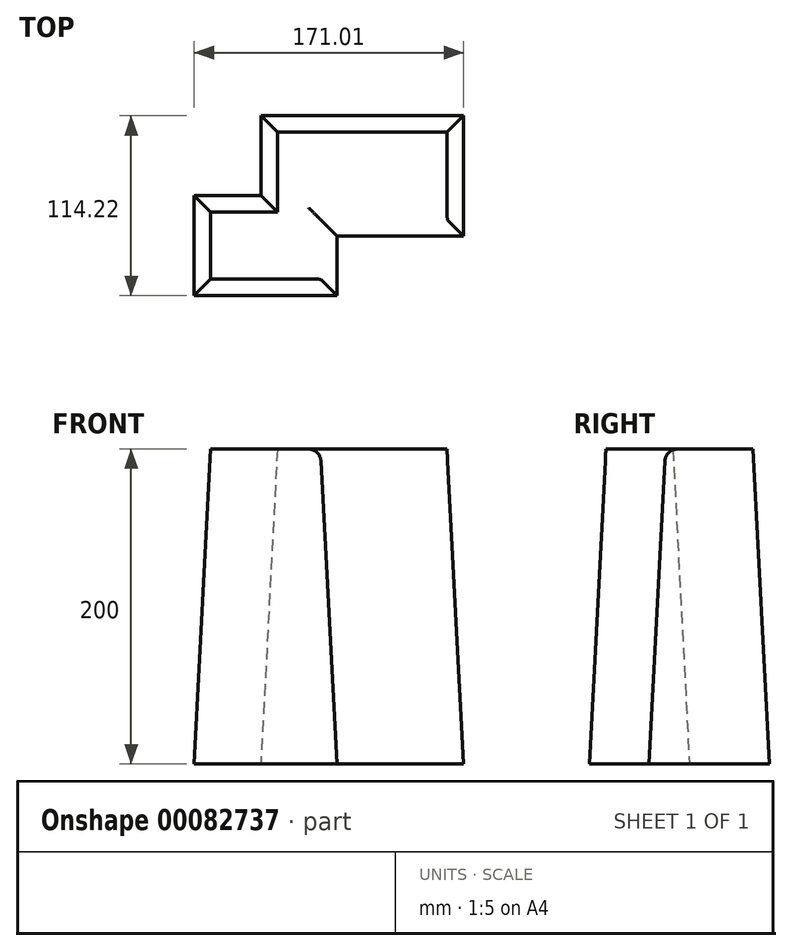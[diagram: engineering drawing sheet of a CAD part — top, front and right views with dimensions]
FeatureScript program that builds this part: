
annotation { "Feature Type Name" : "Feature", "Feature Type Description" : "" }
export const myFeature = defineFeature(function(context is Context, id is Id, definition is map)
    precondition{}
    {
        {
            var Q0;
            Q0=qCreatedBy(makeId("Top.planeOp"),FACE);
            var sketch = newSketch(context, id + "F0", { "sketchPlane" : qUnion([Q0])});
            skLineSegment(sketch, "E0.bottom", {"start": v(0, 0) * mm, "end": v(90.56, 0) * mm});
            skLineSegment(sketch, "E0.top", {"start": v(0, 63.51) * mm, "end": v(42.33, 63.51) * mm});
            skLineSegment(sketch, "E0.left", {"start": v(0, 0) * mm, "end": v(0, 63.51) * mm});
            skLineSegment(sketch, "E0.right", {"start": v(90.56, 0) * mm, "end": v(90.56, 37.82) * mm});
            skLineSegment(sketch, "E1.bottom", {"start": v(90.56, 37.82) * mm, "end": v(171.01, 37.82) * mm});
            skLineSegment(sketch, "E1.top", {"start": v(42.33, 114.22) * mm, "end": v(171.01, 114.22) * mm});
            skLineSegment(sketch, "E1.left", {"start": v(42.33, 63.51) * mm, "end": v(42.33, 114.22) * mm});
            skLineSegment(sketch, "E1.right", {"start": v(171.01, 37.82) * mm, "end": v(171.01, 114.22) * mm});
            skSolve(sketch);
        }
        {
            var Q0;
            Q0 = qSketchRegion(id + "F0", true);
            extrude(context, id + "F1", {"entities" : qUnion([Q0]), "depth" : 200 * mm, "hasDraft" : true, "draftAngle" : 3 * degree, "draftPullDirection" : true});
        }
        {
            var Q0;
            Q0=makeQuery(id+"F1.opExtrude","CAP_EDGE",EDGE,{"disambiguationData":[OSD([sQuery(id+"F0.wireOp",EDGE,"E0.right")])],"isStart":false});
            fillet(context, id + "F2", {"entities" : qUnion([Q0]), "radius" : 8 * mm, "tangentPropagation" : true, "allowEdgeOverflow" : false});
        }
        {
            var Q0;
            Q0=makeQuery(id+"F1.opExtrude","CAP_EDGE",EDGE,{"disambiguationData":[OSD([sQuery(id+"F0.wireOp",EDGE,"E1.bottom")])],"isStart":false});
            fillet(context, id + "F3", {"entities" : qUnion([Q0]), "radius" : 8 * mm, "tangentPropagation" : true, "allowEdgeOverflow" : false});
        }
    });
